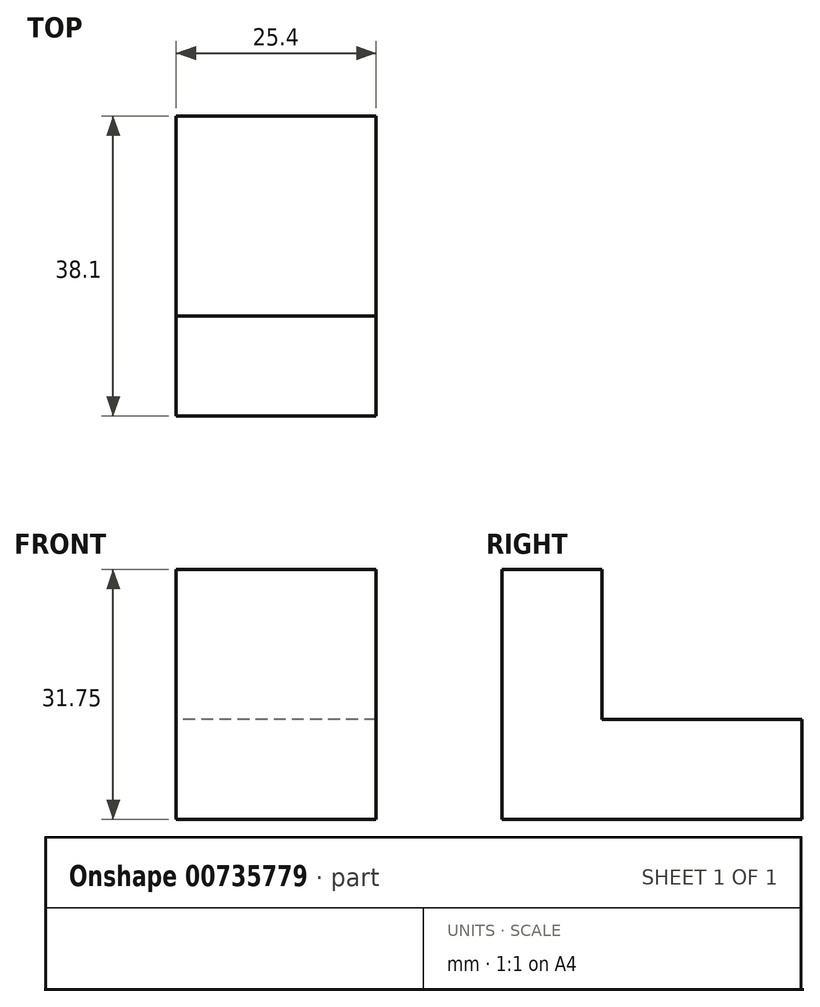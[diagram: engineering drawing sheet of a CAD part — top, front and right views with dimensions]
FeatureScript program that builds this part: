
annotation { "Feature Type Name" : "Feature", "Feature Type Description" : "" }
export const myFeature = defineFeature(function(context is Context, id is Id, definition is map)
    precondition{}
    {
        {
            var Q0;
            Q0=qCreatedBy(makeId("Right.planeOp"),FACE);
            var sketch = newSketch(context, id + "F0", { "sketchPlane" : qUnion([Q0])});
            skLineSegment(sketch, "E0", {"start": v(0, 0) * mm, "end": v(38.1, 0) * mm});
            skLineSegment(sketch, "E1", {"start": v(38.1, 0) * mm, "end": v(38.1, 12.7) * mm});
            skLineSegment(sketch, "E2", {"start": v(38.1, 12.7) * mm, "end": v(12.7, 12.7) * mm});
            skLineSegment(sketch, "E3", {"start": v(12.7, 12.7) * mm, "end": v(12.7, 31.75) * mm});
            skLineSegment(sketch, "E4", {"start": v(12.7, 31.75) * mm, "end": v(0, 31.75) * mm});
            skLineSegment(sketch, "E5", {"start": v(0, 31.75) * mm, "end": v(0, 0) * mm});
            skSolve(sketch);
        }
        {
            var Q0;
            Q0=makeQuery(id+"F0.imprint","IMPRINT",FACE,{"disambiguationData":[TD([[makeQuery(id+"F0.imprint","IMPRINT",EDGE,{"derivedFrom":sQuery(id+"F0.wireOp",EDGE,"E0")}),1.0]])]});
            extrude(context, id + "F1", {"entities" : qUnion([Q0]), "depth" : 25.4 * mm, "offsetDistance" : 25.4 * mm});
        }
    });
